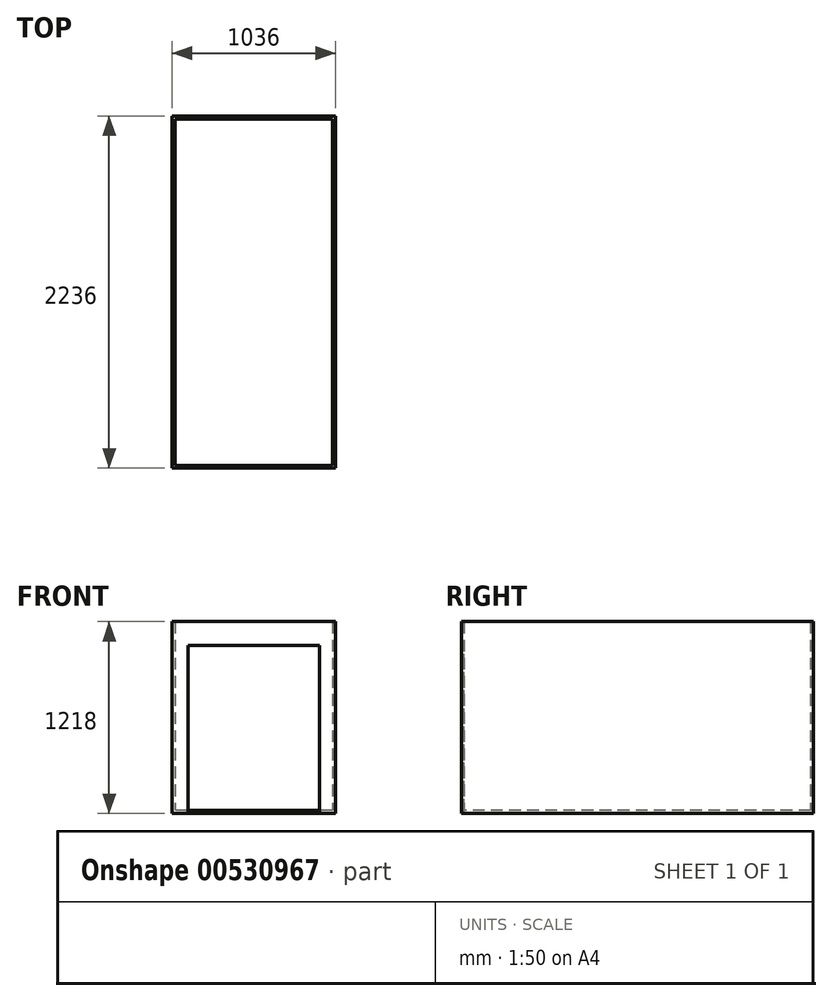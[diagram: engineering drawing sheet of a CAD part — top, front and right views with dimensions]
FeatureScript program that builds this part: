
annotation { "Feature Type Name" : "Feature", "Feature Type Description" : "" }
export const myFeature = defineFeature(function(context is Context, id is Id, definition is map)
    precondition{}
    {
        {
            var Q0;
            Q0=qCreatedBy(makeId("Top.planeOp"),FACE);
            var sketch = newSketch(context, id + "F0", { "sketchPlane" : qUnion([Q0])});
            skLineSegment(sketch, "E0.bottom", {"start": v(1036, 2236) * mm, "end": v(0, 2236) * mm});
            skLineSegment(sketch, "E0.top", {"start": v(1036, 0) * mm, "end": v(0, 0) * mm});
            skLineSegment(sketch, "E0.left", {"start": v(1036, 2236) * mm, "end": v(1036, 0) * mm});
            skLineSegment(sketch, "E0.right", {"start": v(0, 2236) * mm, "end": v(0, 0) * mm});
            skLineSegment(sketch, "E1.bottom", {"start": v(1018, 2218) * mm, "end": v(18, 2218) * mm});
            skLineSegment(sketch, "E1.top", {"start": v(1018, 18) * mm, "end": v(18, 18) * mm});
            skLineSegment(sketch, "E1.left", {"start": v(1018, 2218) * mm, "end": v(1018, 18) * mm});
            skLineSegment(sketch, "E1.right", {"start": v(18, 2218) * mm, "end": v(18, 18) * mm});
            skPoint(sketch, "E1.middle", {"position": v(518, 1118) * mm});
            skSolve(sketch);
        }
        {
            var Q0;
            Q0 = qSketchRegion(id + "F0", true);
            extrude(context, id + "F1", {"entities" : qUnion([Q0]), "depth" : 1200 * mm, "offsetDistance" : 25 * mm});
        }
        {
            var Q0;
            Q0=makeQuery(id+"F1.opExtrude","CAP_FACE",FACE,{"disambiguationData":[OSD([sQuery(id+"F0.wireOp",EDGE,"E0.bottom"),sQuery(id+"F0.wireOp",EDGE,"E0.top"),sQuery(id+"F0.wireOp",EDGE,"E0.left"),sQuery(id+"F0.wireOp",EDGE,"E0.right"),sQuery(id+"F0.wireOp",EDGE,"E1.bottom"),sQuery(id+"F0.wireOp",EDGE,"E1.top"),sQuery(id+"F0.wireOp",EDGE,"E1.left"),sQuery(id+"F0.wireOp",EDGE,"E1.right")])],"isStart":true});
            var sketch = newSketch(context, id + "F2", { "sketchPlane" : qUnion([Q0])});
            skLineSegment(sketch, "E2.bottom", {"start": v(0, 0) * mm, "end": v(1036, 0) * mm});
            skLineSegment(sketch, "E2.top", {"start": v(0, -2236) * mm, "end": v(1036, -2236) * mm});
            skLineSegment(sketch, "E2.left", {"start": v(0, 0) * mm, "end": v(0, -2236) * mm});
            skLineSegment(sketch, "E2.right", {"start": v(1036, 0) * mm, "end": v(1036, -2236) * mm});
            skSolve(sketch);
        }
        {
            var Q0;
            Q0 = qSketchRegion(id + "F2", true);
            extrude(context, id + "F3", {"entities" : qUnion([Q0]), "operationType" : NewBodyOperationType.ADD, "depth" : 18 * mm, "offsetDistance" : 25 * mm});
        }
        {
            var Q0;
            Q0=makeQuery(id+"F3.boolean.opBoolean","MERGE",FACE,{"derivedFrom":[makeQuery(id+"F1.opExtrude","SWEPT_FACE",FACE,{"disambiguationData":[OSD([sQuery(id+"F0.wireOp",EDGE,"E0.top")])]}),makeQuery(id+"F3.opExtrude","SWEPT_FACE",FACE,{"disambiguationData":[OSD([sQuery(id+"F2.wireOp",EDGE,"E2.bottom")])]})]});
            var sketch = newSketch(context, id + "F4", { "sketchPlane" : qUnion([Q0])});
            skLineSegment(sketch, "E3.bottom", {"start": v(100, -18) * mm, "end": v(936, -18) * mm});
            skLineSegment(sketch, "E3.top", {"start": v(100, 1050) * mm, "end": v(936, 1050) * mm});
            skLineSegment(sketch, "E3.left", {"start": v(100, -18) * mm, "end": v(100, 1050) * mm});
            skLineSegment(sketch, "E3.right", {"start": v(936, -18) * mm, "end": v(936, 1050) * mm});
            skPoint(sketch, "E3.middle", {"position": v(518, 516) * mm});
            skLineSegment(sketch, "E4", {"start": v(518, 516) * mm, "end": v(0, 591) * mm, "construction": true});
            skSolve(sketch);
        }
        {
            var Q0;
            Q0 = qSketchRegion(id + "F4", true);
            extrude(context, id + "F5", {"entities" : qUnion([Q0]), "operationType" : NewBodyOperationType.REMOVE, "oppositeDirection" : true, "depth" : 18 * mm, "offsetDistance" : 25 * mm});
        }
    });
